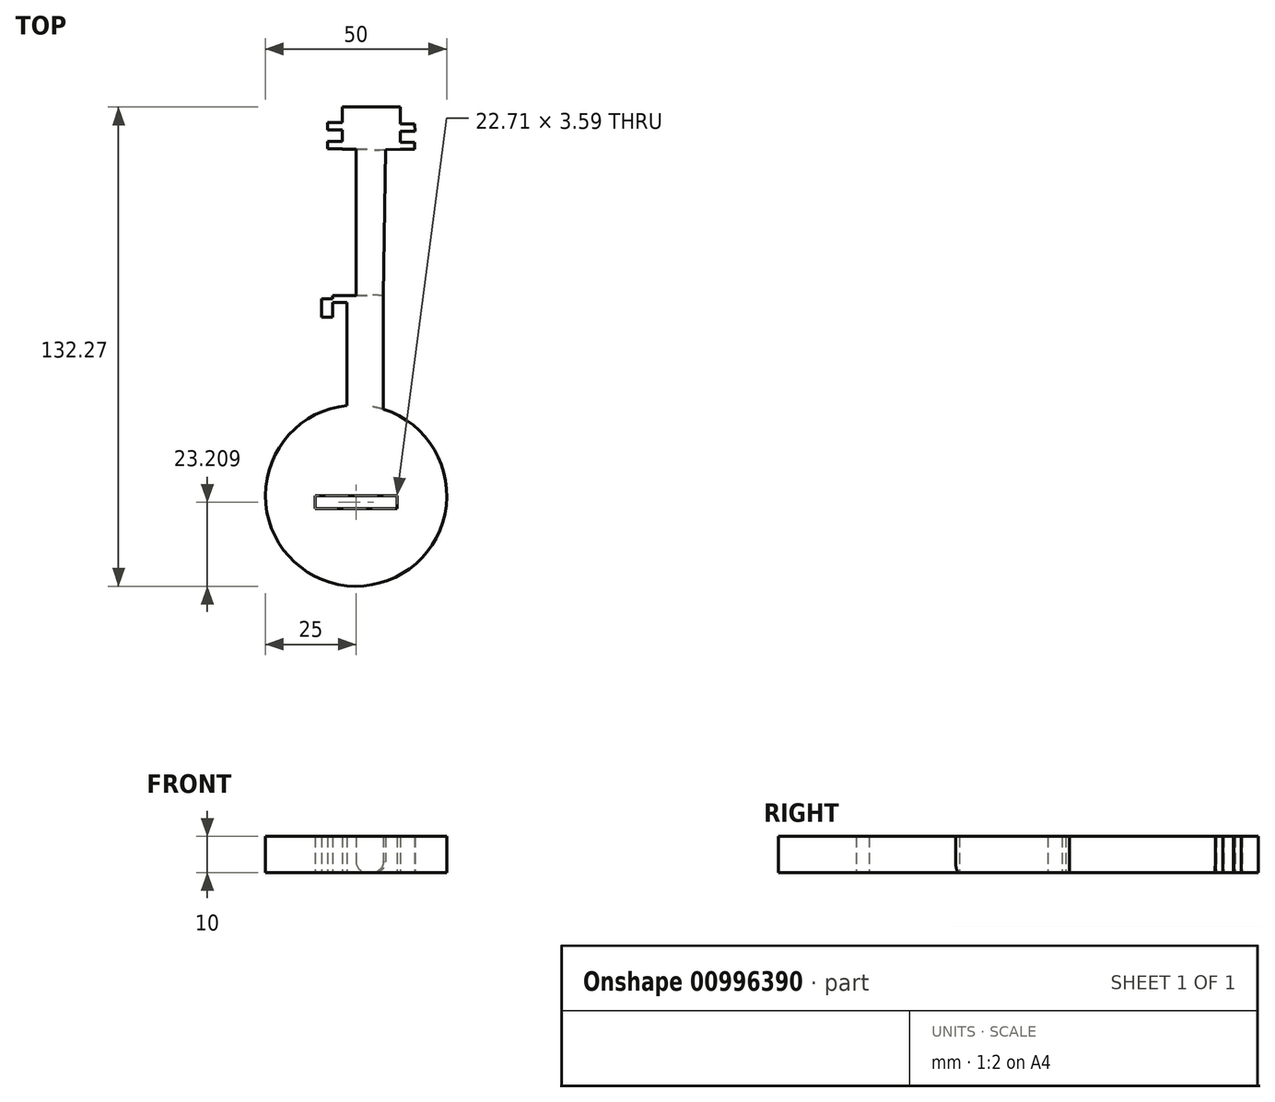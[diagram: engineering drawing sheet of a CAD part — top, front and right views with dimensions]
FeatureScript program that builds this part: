
annotation { "Feature Type Name" : "Feature", "Feature Type Description" : "" }
export const myFeature = defineFeature(function(context is Context, id is Id, definition is map)
    precondition{}
    {
        {
            var Q0;
            Q0=qCreatedBy(makeId("Top.planeOp"),FACE);
            var sketch = newSketch(context, id + "F0", { "sketchPlane" : qUnion([Q0])});
            skCircle(sketch, "E0", {"center": v(0, -35.92) * mm, "radius": 25 * mm});
            skLineSegment(sketch, "E1", {"start": v(-2.48, -11.04) * mm, "end": v(-2.48, 19.35) * mm});
            skLineSegment(sketch, "E2", {"start": v(-2.48, 19.35) * mm, "end": v(7.52, 19.35) * mm});
            skLineSegment(sketch, "E3", {"start": v(7.52, 19.35) * mm, "end": v(7.52, -12.07) * mm});
            skLineSegment(sketch, "E4", {"start": v(8.14, 59.53) * mm, "end": v(7.52, 19.35) * mm});
            skLineSegment(sketch, "E5", {"start": v(0, 59.64) * mm, "end": v(0, 19.35) * mm});
            skLineSegment(sketch, "E6", {"start": v(0, 59.64) * mm, "end": v(8.14, 59.53) * mm});
            skLineSegment(sketch, "E7", {"start": v(0, 59.64) * mm, "end": v(-3.82, 59.64) * mm});
            skLineSegment(sketch, "E8", {"start": v(-3.82, 59.64) * mm, "end": v(-3.82, 71.35) * mm});
            skLineSegment(sketch, "E9", {"start": v(-3.82, 71.35) * mm, "end": v(12.18, 71.35) * mm});
            skLineSegment(sketch, "E10", {"start": v(12.18, 71.35) * mm, "end": v(12.18, 59.64) * mm});
            skLineSegment(sketch, "E11", {"start": v(12.18, 59.64) * mm, "end": v(8.14, 59.53) * mm});
            skLineSegment(sketch, "E12", {"start": v(-3.82, 67) * mm, "end": v(-7.82, 67) * mm});
            skLineSegment(sketch, "E13", {"start": v(-7.82, 67) * mm, "end": v(-7.82, 65) * mm});
            skLineSegment(sketch, "E14", {"start": v(-7.82, 65) * mm, "end": v(-3.82, 65) * mm});
            skLineSegment(sketch, "E15", {"start": v(-3.82, 61.87) * mm, "end": v(-7.82, 61.87) * mm});
            skLineSegment(sketch, "E16", {"start": v(-7.82, 61.87) * mm, "end": v(-7.82, 59.87) * mm});
            skLineSegment(sketch, "E17", {"start": v(-7.82, 59.87) * mm, "end": v(-3.82, 59.87) * mm});
            skLineSegment(sketch, "E18", {"start": v(12.18, 66.7) * mm, "end": v(16.18, 66.7) * mm});
            skLineSegment(sketch, "E19", {"start": v(16.18, 66.7) * mm, "end": v(16.24, 64.7) * mm});
            skLineSegment(sketch, "E20", {"start": v(16.24, 64.7) * mm, "end": v(12.18, 64.59) * mm});
            skLineSegment(sketch, "E21", {"start": v(12.18, 64.59) * mm, "end": v(12.18, 61.54) * mm});
            skLineSegment(sketch, "E22", {"start": v(12.18, 61.54) * mm, "end": v(16.18, 61.64) * mm});
            skLineSegment(sketch, "E23", {"start": v(16.18, 61.64) * mm, "end": v(16.18, 59.64) * mm});
            skLineSegment(sketch, "E24", {"start": v(16.18, 59.64) * mm, "end": v(12.18, 59.64) * mm});
            skLineSegment(sketch, "E25", {"start": v(-6.48, 19.35) * mm, "end": v(-6.48, 17.35) * mm});
            skLineSegment(sketch, "E26", {"start": v(-6.48, 17.35) * mm, "end": v(-2.48, 17.35) * mm});
            skLineSegment(sketch, "E27", {"start": v(-2.48, 19.35) * mm, "end": v(-6.48, 19.35) * mm});
            skLineSegment(sketch, "E28", {"start": v(-11.35, -39.5) * mm, "end": v(-11.35, -35.92) * mm});
            skLineSegment(sketch, "E29.MirrorCS", {"start": v(11.35, -35.92) * mm, "end": v(-11.35, -35.92) * mm});
            skLineSegment(sketch, "E30.MirrorCS", {"start": v(-11.35, -39.5) * mm, "end": v(11.35, -39.5) * mm});
            skLineSegment(sketch, "E31.MirrorCS", {"start": v(11.35, -39.5) * mm, "end": v(11.35, -35.92) * mm});
            skLineSegment(sketch, "E32.MirrorCS", {"start": v(-11.35, -35.92) * mm, "end": v(11.35, -35.92) * mm});
            skLineSegment(sketch, "E33.MirrorCS", {"start": v(11.35, -39.5) * mm, "end": v(-11.35, -39.5) * mm});
            skLineSegment(sketch, "E34", {"start": v(-4, -60.6) * mm, "end": v(-4, -51.64) * mm});
            skLineSegment(sketch, "E35", {"start": v(-4, -51.64) * mm, "end": v(0, -51.64) * mm});
            skLineSegment(sketch, "E36.MirrorCS", {"start": v(4, -60.6) * mm, "end": v(4, -51.64) * mm});
            skLineSegment(sketch, "E37.MirrorCS", {"start": v(4, -51.64) * mm, "end": v(0, -51.64) * mm});
            skLineSegment(sketch, "E38", {"start": v(-6.48, 18.38) * mm, "end": v(-6.48, 19.35) * mm});
            skLineSegment(sketch, "E39", {"start": v(-6.48, 18.38) * mm, "end": v(-9.48, 18.38) * mm});
            skLineSegment(sketch, "E40", {"start": v(-9.48, 18.38) * mm, "end": v(-9.48, 13.38) * mm});
            skLineSegment(sketch, "E41", {"start": v(-9.48, 13.38) * mm, "end": v(-6.48, 13.38) * mm});
            skLineSegment(sketch, "E42", {"start": v(-6.48, 13.38) * mm, "end": v(-6.48, 17.35) * mm});
            skSolve(sketch);
        }
        {
            var Q0;
            Q0 = qSketchRegion(id + "F0", true);
            extrude(context, id + "F1", {"entities" : qUnion([Q0]), "depth" : 10 * mm, "offsetDistance" : 25 * mm});
        }
        {
            var Q0;
            Q0=makeQuery(id+"F1.opExtrude","CAP_EDGE",EDGE,{"disambiguationData":[OSD([sQuery(id+"F0.wireOp",EDGE,"E5")])],"isStart":true});
            var Q1;
            Q1=makeQuery(id+"F1.opExtrude","CAP_EDGE",EDGE,{"disambiguationData":[OSD([sQuery(id+"F0.wireOp",EDGE,"E4")])],"isStart":true});
            fillet(context, id + "F2", {"entities" : qUnion([Q0, Q1]), "radius" : 3 * mm, "tangentPropagation" : true, "allowEdgeOverflow" : false});
        }
    });
